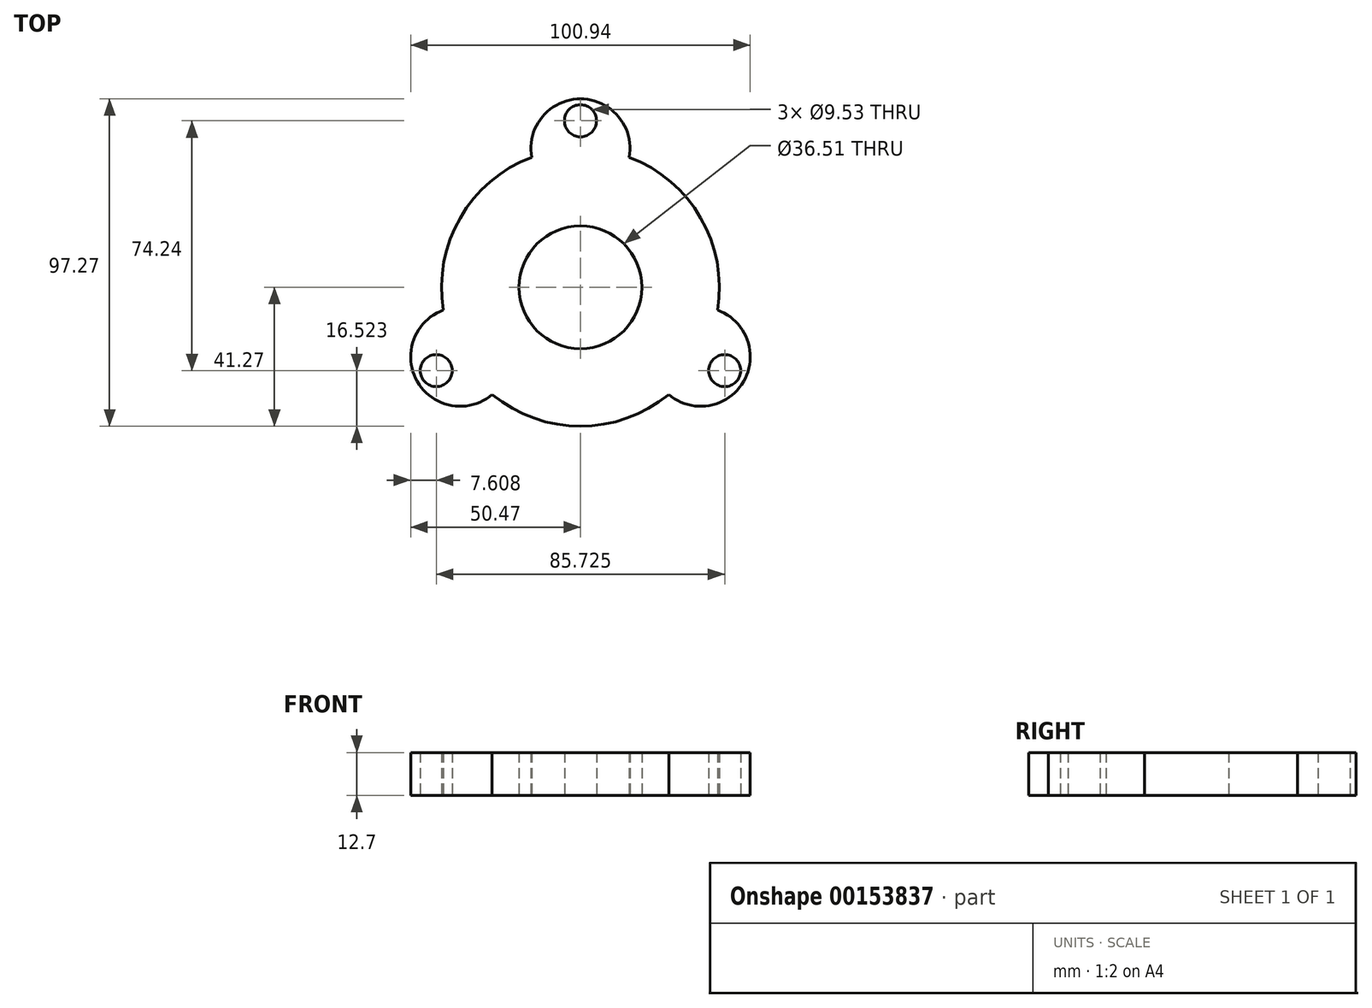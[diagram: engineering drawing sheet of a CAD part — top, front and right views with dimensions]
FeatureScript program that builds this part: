
annotation { "Feature Type Name" : "Feature", "Feature Type Description" : "" }
export const myFeature = defineFeature(function(context is Context, id is Id, definition is map)
    precondition{}
    {
        {
            var Q0;
            Q0=qCreatedBy(makeId("Top.planeOp"),FACE);
            var sketch = newSketch(context, id + "F0", { "sketchPlane" : qUnion([Q0])});
            skCircle(sketch, "E0", {"center": v(0, 0) * mm, "radius": 18.26 * mm});
            skCircle(sketch, "E1", {"center": v(0, 49.5) * mm, "radius": 4.76 * mm});
            skCircle(sketch, "E2.1.0", {"center": v(-42.86, -24.75) * mm, "radius": 4.76 * mm});
            skCircle(sketch, "E2.2.0", {"center": v(42.86, -24.75) * mm, "radius": 4.76 * mm});
            skLineSegment(sketch, "E3", {"start": v(0, 49.5) * mm, "end": v(0, 0) * mm, "construction": true});
            skCircle(sketch, "E4", {"center": v(0, 0) * mm, "radius": 41.28 * mm});
            skArc(sketch, "E5", {"start": v(14.49, 38.65) * mm, "mid": v(0, 56) * mm, "end": v(-14.49, 38.65) * mm});
            skArc(sketch, "E6.1.0", {"start": v(-40.71, -6.78) * mm, "mid": v(-48.5, -28) * mm, "end": v(-26.23, -31.87) * mm});
            skArc(sketch, "E6.2.0", {"start": v(26.23, -31.87) * mm, "mid": v(48.5, -28) * mm, "end": v(40.71, -6.78) * mm});
            skSolve(sketch);
        }
        {
            var Q0;
            Q0=makeQuery(id+"F0.imprint","IMPRINT",FACE,{"disambiguationData":[TD([[makeQuery(id+"F0.imprint","IMPRINT",EDGE,{"derivedFrom":sQuery(id+"F0.wireOp",EDGE,"E0")}),-1.0]])]});
            var Q1;
            Q1=makeQuery(id+"F0.imprint","IMPRINT",FACE,{"disambiguationData":[TD([[makeQuery(id+"F0.imprint","IMPRINT",EDGE,{"derivedFrom":sQuery(id+"F0.wireOp",EDGE,"E2.1.0")}),-1.0]])]});
            var Q2;
            Q2=makeQuery(id+"F0.imprint","IMPRINT",FACE,{"disambiguationData":[TD([[makeQuery(id+"F0.imprint","IMPRINT",EDGE,{"derivedFrom":sQuery(id+"F0.wireOp",EDGE,"E1")}),-1.0]])]});
            var Q3;
            Q3=makeQuery(id+"F0.imprint","IMPRINT",FACE,{"disambiguationData":[TD([[makeQuery(id+"F0.imprint","IMPRINT",EDGE,{"derivedFrom":sQuery(id+"F0.wireOp",EDGE,"E2.2.0")}),-1.0]])]});
            extrude(context, id + "F1", {"entities" : qUnion([Q0, Q1, Q2, Q3]), "depth" : 12.7 * mm});
        }
    });
